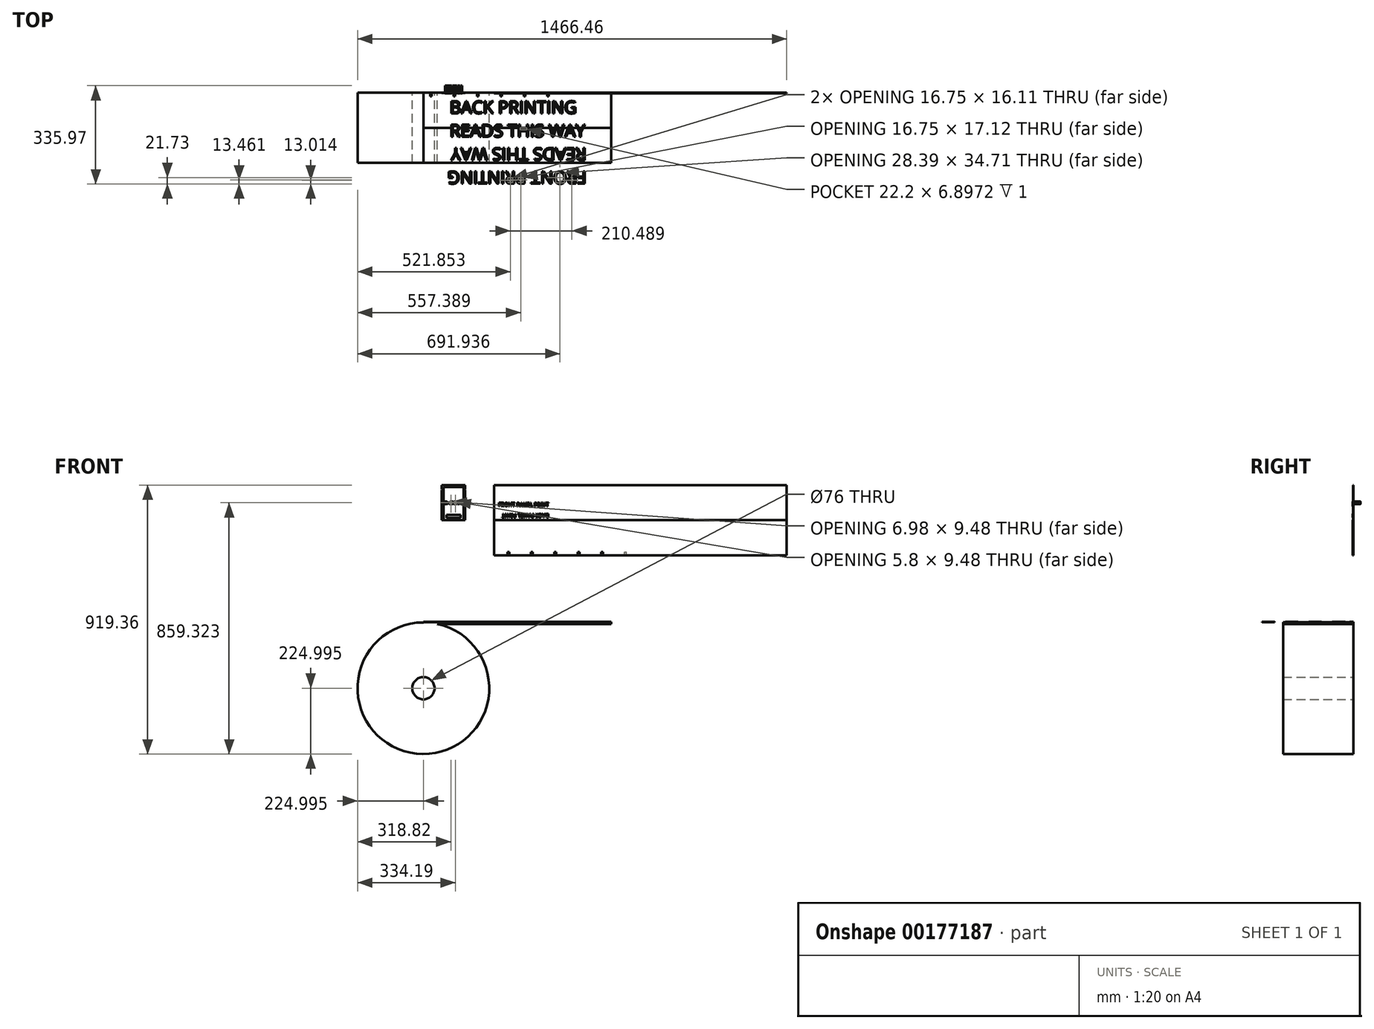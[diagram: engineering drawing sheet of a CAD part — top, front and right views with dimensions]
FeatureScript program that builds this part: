
annotation { "Feature Type Name" : "Feature", "Feature Type Description" : "" }
export const myFeature = defineFeature(function(context is Context, id is Id, definition is map)
    precondition{}
    {
        {
            assignVariable(context, id + "F0", {"name" : "hoogte", "anyValue" : 120});
        }
        {
            var Q0;
            Q0=qCreatedBy(makeId("Front.planeOp"),FACE);
            var sketch = newSketch(context, id + "F1", { "sketchPlane" : qUnion([Q0])});
            skLineSegment(sketch, "E0.bottom", {"start": v(-40, 60) * mm, "end": v(40, 60) * mm});
            skLineSegment(sketch, "E0.top", {"start": v(-40, -60) * mm, "end": v(40, -60) * mm});
            skLineSegment(sketch, "E0.left", {"start": v(-40, 60) * mm, "end": v(-40, -60) * mm});
            skLineSegment(sketch, "E0.right", {"start": v(40, 60) * mm, "end": v(40, -60) * mm});
            skLineSegment(sketch, "E1", {"start": v(-40, 46.41) * mm, "end": v(-38.59, 45) * mm});
            skLineSegment(sketch, "E2", {"start": v(-38.59, 45) * mm, "end": v(-40, 43.59) * mm});
            skLineSegment(sketch, "E3", {"start": v(40, 46.41) * mm, "end": v(38.59, 45) * mm});
            skLineSegment(sketch, "E4", {"start": v(38.59, 45) * mm, "end": v(40, 43.59) * mm});
            skLineSegment(sketch, "E5.bottom", {"start": v(138.46, 60) * mm, "end": v(1138.46, 60) * mm});
            skLineSegment(sketch, "E5.top", {"start": v(138.46, -180) * mm, "end": v(1138.46, -180) * mm});
            skLineSegment(sketch, "E5.left", {"start": v(138.46, 60) * mm, "end": v(138.46, -180) * mm});
            skLineSegment(sketch, "E5.right", {"start": v(1138.46, 60) * mm, "end": v(1138.46, -180) * mm});
            skLineSegment(sketch, "E6", {"start": v(138.46, -60) * mm, "end": v(1138.46, -60) * mm});
            skLineSegment(sketch, "E7", {"start": v(-40, 60) * mm, "end": v(40, -60) * mm, "construction": true});
            skLineSegment(sketch, "E8", {"start": v(40, 60) * mm, "end": v(-40, -60) * mm, "construction": true});
            skPoint(sketch, "E9", {"position": v(0, 0) * mm});
            skSolve(sketch);
        }
        {
            var Q0;
            {var subQ3=sQuery(id+"F1.wireOp",EDGE,"E0.bottom");Q0=makeQuery(id+"F1.imprint","IMPRINT",FACE,{"disambiguationData":[TD([[makeQuery(id+"F1.imprint","IMPRINT",EDGE,{"derivedFrom":subQ3}),-1.0]])]});}
            var Q1;
            Q1=makeQuery(id+"F1.imprint","IMPRINT",FACE,{"disambiguationData":[TD([[makeQuery(id+"F1.imprint","IMPRINT",EDGE,{"derivedFrom":sQuery(id+"F1.wireOp",EDGE,"E5.bottom")}),-1.0]])]});
            var Q2;
            {var subQ0=sQuery(id+"F1.wireOp",EDGE,"E5.top");Q2=makeQuery(id+"F1.imprint","IMPRINT",FACE,{"disambiguationData":[TD([[makeQuery(id+"F1.imprint","IMPRINT",EDGE,{"derivedFrom":subQ0}),1.0]])]});}
            extrude(context, id + "F2", {"entities" : qUnion([Q0, Q1, Q2]), "depth" : 1 * mm});
        }
        {
            var Q0;
            Q0=makeQuery(id+"F2.opExtrude","CAP_FACE",FACE,{"disambiguationData":[OSD([sQuery(id+"F1.wireOp",EDGE,"E0.bottom"),sQuery(id+"F1.wireOp",EDGE,"E0.top"),sQuery(id+"F1.wireOp",EDGE,"E0.left"),sQuery(id+"F1.wireOp",EDGE,"E0.right"),sQuery(id+"F1.wireOp",EDGE,"E1"),sQuery(id+"F1.wireOp",EDGE,"E2"),sQuery(id+"F1.wireOp",EDGE,"E3"),sQuery(id+"F1.wireOp",EDGE,"E4")])],"isStart":false});
            var sketch = newSketch(context, id + "F3", { "sketchPlane" : qUnion([Q0])});
            skLineSegment(sketch, "E10.0.0", {"start": v(40, 60) * mm, "end": v(-40, 60) * mm});
            skLineSegment(sketch, "E10.0.1", {"start": v(-40, 60) * mm, "end": v(-40, 46.41) * mm});
            skLineSegment(sketch, "E10.0.2", {"start": v(-40, 46.41) * mm, "end": v(-38.59, 45) * mm});
            skLineSegment(sketch, "E10.0.3", {"start": v(-38.59, 45) * mm, "end": v(-40, 43.59) * mm});
            skLineSegment(sketch, "E10.0.4", {"start": v(-40, 43.59) * mm, "end": v(-40, -60) * mm});
            skLineSegment(sketch, "E10.0.5", {"start": v(-40, -60) * mm, "end": v(40, -60) * mm});
            skLineSegment(sketch, "E10.0.6", {"start": v(40, -60) * mm, "end": v(40, 43.59) * mm});
            skLineSegment(sketch, "E10.0.7", {"start": v(40, 43.59) * mm, "end": v(38.59, 45) * mm});
            skLineSegment(sketch, "E10.0.8", {"start": v(38.59, 45) * mm, "end": v(40, 46.41) * mm});
            skLineSegment(sketch, "E10.0.9", {"start": v(40, 46.41) * mm, "end": v(40, 60) * mm});
            skLineSegment(sketch, "E11.bottom", {"start": v(-34, 54) * mm, "end": v(34, 54) * mm});
            skLineSegment(sketch, "E11.top", {"start": v(-34, -59.99) * mm, "end": v(34, -59.99) * mm});
            skLineSegment(sketch, "E11.left", {"start": v(-34, 54) * mm, "end": v(-34, -59.99) * mm});
            skLineSegment(sketch, "E11.right", {"start": v(34, 54) * mm, "end": v(34, -59.99) * mm});
            skLineSegment(sketch, "E12.bottom", {"start": v(-40, 60) * mm, "end": v(-37, 60) * mm});
            skLineSegment(sketch, "E12.top", {"start": v(-40, 48) * mm, "end": v(-37, 48) * mm});
            skLineSegment(sketch, "E12.left", {"start": v(-40, 60) * mm, "end": v(-40, 48) * mm});
            skLineSegment(sketch, "E12.right", {"start": v(-37, 60) * mm, "end": v(-37, 48) * mm});
            skLineSegment(sketch, "E13.bottom", {"start": v(40, 60) * mm, "end": v(37, 60) * mm});
            skLineSegment(sketch, "E13.top", {"start": v(40, 48) * mm, "end": v(37, 48) * mm});
            skLineSegment(sketch, "E13.left", {"start": v(40, 60) * mm, "end": v(40, 48) * mm});
            skLineSegment(sketch, "E13.right", {"start": v(37, 60) * mm, "end": v(37, 48) * mm});
            skLineSegment(sketch, "E14.bottom", {"start": v(-24, -42) * mm, "end": v(24, -42) * mm});
            skLineSegment(sketch, "E14.top", {"start": v(-24, -52) * mm, "end": v(24, -52) * mm});
            skLineSegment(sketch, "E14.left", {"start": v(-24, -42) * mm, "end": v(-24, -52) * mm});
            skLineSegment(sketch, "E14.right", {"start": v(24, -42) * mm, "end": v(24, -52) * mm});
            skSolve(sketch);
        }
        {
            var Q0;
            Q0=makeQuery(id+"F3.imprint","IMPRINT",FACE,{"disambiguationData":[TD([[makeQuery(id+"F3.imprint","IMPRINT",EDGE,{"derivedFrom":sQuery(id+"F3.wireOp",EDGE,"E11.bottom")}),-1.0]])]});
            var Q1;
            Q1=makeQuery(id+"F3.imprint","IMPRINT",FACE,{"disambiguationData":[TD([[makeQuery(id+"F3.imprint","IMPRINT",EDGE,{"derivedFrom":sQuery(id+"F3.wireOp",EDGE,"E12.bottom")}),-1.0]])]});
            var Q2;
            Q2=makeQuery(id+"F3.imprint","IMPRINT",FACE,{"disambiguationData":[TD([[makeQuery(id+"F3.imprint","IMPRINT",EDGE,{"derivedFrom":sQuery(id+"F3.wireOp",EDGE,"E13.bottom")}),-1.0]])]});
            extrude(context, id + "F4", {"entities" : qUnion([Q0, Q1, Q2]), "operationType" : NewBodyOperationType.REMOVE, "oppositeDirection" : true, "depth" : 0.5 * mm});
        }
        {
            var Q0;
            Q0=makeQuery(id+"F2.opExtrude","CAP_FACE",FACE,{"disambiguationData":[OSD([sQuery(id+"F1.wireOp",EDGE,"E5.bottom"),sQuery(id+"F1.wireOp",EDGE,"E5.left"),sQuery(id+"F1.wireOp",EDGE,"E5.right"),sQuery(id+"F1.wireOp",EDGE,"E6")])],"isStart":false});
            var sketch = newSketch(context, id + "F5", { "sketchPlane" : qUnion([Q0])});
            skLineSegment(sketch, "E15.0.0", {"start": v(1138.46, 60) * mm, "end": v(138.46, 60) * mm});
            skLineSegment(sketch, "E15.0.1", {"start": v(138.46, 60) * mm, "end": v(138.46, 60) * mm});
            skLineSegment(sketch, "E15.0.2", {"start": v(138.46, 60) * mm, "end": v(1138.46, 60) * mm});
            skLineSegment(sketch, "E15.0.3", {"start": v(1138.46, 60) * mm, "end": v(1138.46, 60) * mm});
            skLineSegment(sketch, "E16.bottom", {"start": v(184.68, -180) * mm, "end": v(190.68, -180) * mm});
            skLineSegment(sketch, "E16.top", {"start": v(184.68, -168) * mm, "end": v(190.68, -168) * mm});
            skLineSegment(sketch, "E16.left", {"start": v(184.68, -180) * mm, "end": v(184.68, -168) * mm});
            skLineSegment(sketch, "E16.right", {"start": v(190.68, -180) * mm, "end": v(190.68, -168) * mm});
            skLineSegment(sketch, "E17.1.0.0", {"start": v(264.68, -168) * mm, "end": v(270.68, -168) * mm});
            skLineSegment(sketch, "E17.1.0.1", {"start": v(264.68, -180) * mm, "end": v(264.68, -168) * mm});
            skLineSegment(sketch, "E17.1.0.2", {"start": v(264.68, -180) * mm, "end": v(270.68, -180) * mm});
            skLineSegment(sketch, "E17.1.0.3", {"start": v(270.68, -180) * mm, "end": v(270.68, -168) * mm});
            skLineSegment(sketch, "E17.2.0.0", {"start": v(344.68, -168) * mm, "end": v(350.68, -168) * mm});
            skLineSegment(sketch, "E17.2.0.1", {"start": v(344.68, -180) * mm, "end": v(344.68, -168) * mm});
            skLineSegment(sketch, "E17.2.0.2", {"start": v(344.68, -180) * mm, "end": v(350.68, -180) * mm});
            skLineSegment(sketch, "E17.2.0.3", {"start": v(350.68, -180) * mm, "end": v(350.68, -168) * mm});
            skLineSegment(sketch, "E17.direction1", {"start": v(184.68, -180) * mm, "end": v(264.68, -180) * mm, "construction": true});
            skLineSegment(sketch, "E18.0.3.0", {"start": v(424.68, -168) * mm, "end": v(430.68, -168) * mm});
            skLineSegment(sketch, "E18.3.3.0", {"start": v(424.68, -180) * mm, "end": v(424.68, -168) * mm});
            skLineSegment(sketch, "E18.6.3.0", {"start": v(424.68, -180) * mm, "end": v(430.68, -180) * mm});
            skLineSegment(sketch, "E18.9.3.0", {"start": v(430.68, -180) * mm, "end": v(430.68, -168) * mm});
            skLineSegment(sketch, "E18.0.4.0", {"start": v(504.68, -168) * mm, "end": v(510.68, -168) * mm});
            skLineSegment(sketch, "E18.3.4.0", {"start": v(504.68, -180) * mm, "end": v(504.68, -168) * mm});
            skLineSegment(sketch, "E18.6.4.0", {"start": v(504.68, -180) * mm, "end": v(510.68, -180) * mm});
            skLineSegment(sketch, "E18.9.4.0", {"start": v(510.68, -180) * mm, "end": v(510.68, -168) * mm});
            skLineSegment(sketch, "E19.0.5.0", {"start": v(584.68, -168) * mm, "end": v(590.68, -168) * mm});
            skLineSegment(sketch, "E19.3.5.0", {"start": v(584.68, -180) * mm, "end": v(584.68, -168) * mm});
            skLineSegment(sketch, "E19.6.5.0", {"start": v(584.68, -180) * mm, "end": v(590.68, -180) * mm});
            skLineSegment(sketch, "E19.9.5.0", {"start": v(590.68, -180) * mm, "end": v(590.68, -168) * mm});
            skSolve(sketch);
        }
        {
            var Q0;
            Q0=makeQuery(id+"F5.imprint","IMPRINT",FACE,{"disambiguationData":[TD([[makeQuery(id+"F5.imprint","IMPRINT",EDGE,{"derivedFrom":sQuery(id+"F5.wireOp",EDGE,"JLQzprwf-iRJq-cmRX-vWmS-HmgRmsplr5sc.top")}),-1.0]])]});
            var Q1;
            Q1=makeQuery(id+"F5.imprint","IMPRINT",FACE,{"disambiguationData":[TD([[makeQuery(id+"F5.imprint","IMPRINT",EDGE,{"derivedFrom":sQuery(id+"F5.wireOp",EDGE,"E16.bottom")}),1.0]])]});
            var Q2;
            Q2=makeQuery(id+"F5.imprint","IMPRINT",FACE,{"disambiguationData":[TD([[makeQuery(id+"F5.imprint","IMPRINT",EDGE,{"derivedFrom":sQuery(id+"F5.wireOp",EDGE,"E17.1.0.0")}),-1.0]])]});
            var Q3;
            Q3=makeQuery(id+"F5.imprint","IMPRINT",FACE,{"disambiguationData":[TD([[makeQuery(id+"F5.imprint","IMPRINT",EDGE,{"derivedFrom":sQuery(id+"F5.wireOp",EDGE,"E17.2.0.0")}),-1.0]])]});
            var Q4;
            Q4=makeQuery(id+"F5.imprint","IMPRINT",FACE,{"disambiguationData":[TD([[makeQuery(id+"F5.imprint","IMPRINT",EDGE,{"derivedFrom":sQuery(id+"F5.wireOp",EDGE,"E18.0.3.0")}),-1.0]])]});
            var Q5;
            Q5=makeQuery(id+"F5.imprint","IMPRINT",FACE,{"disambiguationData":[TD([[makeQuery(id+"F5.imprint","IMPRINT",EDGE,{"derivedFrom":sQuery(id+"F5.wireOp",EDGE,"E18.0.4.0")}),-1.0]])]});
            var Q6;
            Q6=makeQuery(id+"F5.imprint","IMPRINT",FACE,{"disambiguationData":[TD([[makeQuery(id+"F5.imprint","IMPRINT",EDGE,{"derivedFrom":sQuery(id+"F5.wireOp",EDGE,"E19.0.5.0")}),-1.0]])]});
            extrude(context, id + "F6", {"entities" : qUnion([Q0, Q1, Q2, Q3, Q4, Q5, Q6]), "operationType" : NewBodyOperationType.REMOVE, "oppositeDirection" : true, "depth" : 0.5 * mm});
        }
        {
            var Q0;
            Q0=qCreatedBy(makeId("Front.planeOp"),FACE);
            var sketch = newSketch(context, id + "F7", { "sketchPlane" : qUnion([Q0])});
            skCircle(sketch, "E20", {"center": v(-103, -634.36) * mm, "radius": 225 * mm});
            skLineSegment(sketch, "E21.bottom", {"start": v(-103, -408.35) * mm, "end": v(538.87, -408.35) * mm});
            skLineSegment(sketch, "E21.top", {"start": v(-103, -414.51) * mm, "end": v(538.87, -414.51) * mm});
            skLineSegment(sketch, "E21.left", {"start": v(-103, -414.51) * mm, "end": v(-103, -408.35) * mm});
            skLineSegment(sketch, "E21.right", {"start": v(538.87, -414.51) * mm, "end": v(538.87, -408.35) * mm});
            skCircle(sketch, "E22", {"center": v(-103, -634.36) * mm, "radius": 38 * mm});
            skSolve(sketch);
        }
        {
            var Q0;
            Q0=qSketchRegion(id+"F7",true);
            extrude(context, id + "F8", {"entities" : qUnion([Q0]), "depth" : (((getVariable(context, 'hoogte')) * 2)) * mm});
        }
        {
            var Q0;
            {var subQ0=sQuery(id+"F1.wireOp",EDGE,"E4");var subQ1=sQuery(id+"F1.wireOp",EDGE,"E2");var subQ2=sQuery(id+"F1.wireOp",EDGE,"E1");var subQ3=sQuery(id+"F1.wireOp",EDGE,"E0.right");var subQ4=sQuery(id+"F1.wireOp",EDGE,"E0.top");var subQ5=sQuery(id+"F1.wireOp",EDGE,"E0.bottom");var subQ6=sQuery(id+"F1.wireOp",EDGE,"E3");var subQ7=sQuery(id+"F1.wireOp",EDGE,"E0.left");Q0=makeQuery(id+"F4.boolean.opBoolean","SPLIT",FACE,{"disambiguationData":[TD([makeQuery(id+"F2.opExtrude","SWEPT_FACE",FACE,{"disambiguationData":[OSD([subQ5])]})])],"derivedFrom":makeQuery(id+"F2.opExtrude","CAP_FACE",FACE,{"disambiguationData":[OSD([subQ5,subQ4,subQ7,subQ3,subQ2,subQ1,subQ6,subQ0])],"isStart":false})});}
            var sketch = newSketch(context, id + "F9", { "sketchPlane" : qUnion([Q0])});
            skText(sketch, "E23", { "text": "BACKSIDE", "fontName": "OpenSans-Regular.ttf"});
            const initialGuessF9  = {"E23": [-0.03, -0.00465, 1, 0, 0.0093]};
            skSetInitialGuess(sketch, initialGuessF9);
            skSolve(sketch);
        }
        {
            var Q0;
            Q0=qSketchRegion(id+"F9",true);
            extrude(context, id + "F10", {"entities" : qUnion([Q0]), "operationType" : NewBodyOperationType.ADD, "depth" : 1 * mm, "hasSecondDirection" : true, "secondDirectionOppositeDirection" : true, "secondDirectionDepth" : 25 * mm});
        }
        {
            var Q0;
            {var subQ0=sQuery(id+"F1.wireOp",EDGE,"E5.bottom");var subQ1=sQuery(id+"F1.wireOp",EDGE,"E5.left");var subQ2=sQuery(id+"F1.wireOp",EDGE,"E5.right");Q0=makeQuery(id+"F6.boolean.opBoolean","SPLIT",FACE,{"disambiguationData":[TD([makeQuery(id+"F2.opExtrude","SWEPT_FACE",FACE,{"disambiguationData":[OSD([subQ0])]})])],"derivedFrom":makeQuery(id+"F2.opExtrude","CAP_FACE",FACE,{"disambiguationData":[OSD([subQ0,sQuery(id+"F1.wireOp",EDGE,"E5.top"),subQ1,subQ2])],"isStart":false})});}
            var sketch = newSketch(context, id + "F11", { "sketchPlane" : qUnion([Q0])});
            skText(sketch, "E24", { "text": "FRONT PANEL PRINT", "fontName": "AllertaStencil-Regular.ttf"});
            skLineSegment(sketch, "E25.0.0", {"start": v(1138.46, -60) * mm, "end": v(138.46, -60) * mm});
            skLineSegment(sketch, "E25.0.1", {"start": v(138.46, -60) * mm, "end": v(138.46, -180) * mm});
            skLineSegment(sketch, "E25.0.2", {"start": v(138.46, -180) * mm, "end": v(184.68, -180) * mm});
            skLineSegment(sketch, "E25.0.3", {"start": v(184.68, -180) * mm, "end": v(184.68, -168) * mm});
            skLineSegment(sketch, "E25.0.4", {"start": v(184.68, -168) * mm, "end": v(190.68, -168) * mm});
            skLineSegment(sketch, "E25.0.5", {"start": v(190.68, -168) * mm, "end": v(190.68, -180) * mm});
            skLineSegment(sketch, "E25.0.6", {"start": v(190.68, -180) * mm, "end": v(264.68, -180) * mm});
            skLineSegment(sketch, "E25.0.7", {"start": v(264.68, -180) * mm, "end": v(264.68, -168) * mm});
            skLineSegment(sketch, "E25.0.8", {"start": v(264.68, -168) * mm, "end": v(270.68, -168) * mm});
            skLineSegment(sketch, "E25.0.9", {"start": v(270.68, -168) * mm, "end": v(270.68, -180) * mm});
            skLineSegment(sketch, "E25.0.10", {"start": v(270.68, -180) * mm, "end": v(344.68, -180) * mm});
            skLineSegment(sketch, "E25.0.11", {"start": v(344.68, -180) * mm, "end": v(344.68, -168) * mm});
            skLineSegment(sketch, "E25.0.12", {"start": v(344.68, -168) * mm, "end": v(350.68, -168) * mm});
            skLineSegment(sketch, "E25.0.13", {"start": v(350.68, -168) * mm, "end": v(350.68, -180) * mm});
            skLineSegment(sketch, "E25.0.14", {"start": v(350.68, -180) * mm, "end": v(424.68, -180) * mm});
            skLineSegment(sketch, "E25.0.15", {"start": v(424.68, -180) * mm, "end": v(424.68, -168) * mm});
            skLineSegment(sketch, "E25.0.16", {"start": v(424.68, -168) * mm, "end": v(430.68, -168) * mm});
            skLineSegment(sketch, "E25.0.17", {"start": v(430.68, -168) * mm, "end": v(430.68, -180) * mm});
            skLineSegment(sketch, "E25.0.18", {"start": v(430.68, -180) * mm, "end": v(504.68, -180) * mm});
            skLineSegment(sketch, "E25.0.19", {"start": v(504.68, -180) * mm, "end": v(504.68, -168) * mm});
            skLineSegment(sketch, "E25.0.20", {"start": v(504.68, -168) * mm, "end": v(510.68, -168) * mm});
            skLineSegment(sketch, "E25.0.21", {"start": v(510.68, -168) * mm, "end": v(510.68, -180) * mm});
            skLineSegment(sketch, "E25.0.22", {"start": v(510.68, -180) * mm, "end": v(1138.46, -180) * mm});
            skLineSegment(sketch, "E25.0.23", {"start": v(1138.46, -180) * mm, "end": v(1138.46, -60) * mm});
            skText(sketch, "E26", { "text": "BACK PANEL PRINT", "fontName": "AllertaStencil-Regular.ttf"});
            skLineSegment(sketch, "E27", {"start": v(1108.46, -120) * mm, "end": v(1108.46, -121.37) * mm});
            const initialGuessF11  = {"E24": [0.1529, -0.0125, 1, 0, 0.0125], "E26": [0.32596, -0.0375, -1, 0, 0.0125]};
            skSetInitialGuess(sketch, initialGuessF11);
            skSolve(sketch);
        }
        {
            var Q0;
            Q0=qSketchRegion(id+"F11",true);
            extrude(context, id + "F12", {"entities" : qUnion([Q0]), "operationType" : NewBodyOperationType.ADD, "depth" : 1 * mm});
        }
        {
            var Q0;
            Q0=makeQuery(id+"F8.opExtrude","SWEPT_FACE",FACE,{"disambiguationData":[OSD([sQuery(id+"F7.wireOp",EDGE,"E21.bottom")])]});
            var sketch = newSketch(context, id + "F13", { "sketchPlane" : qUnion([Q0])});
            skText(sketch, "E28", { "text": "BACK PRINTING \nREADS THIS WAY", "fontName": "OpenSans-Regular.ttf"});
            skText(sketch, "E29", { "text": "FRONT PRINTING\nREADS THIS WAY", "fontName": "OpenSans-Regular.ttf"});
            skLineSegment(sketch, "E30", {"start": v(478.87, -157.44) * mm, "end": v(478.87, -220) * mm});
            skLineSegment(sketch, "E31", {"start": v(538.87, -120) * mm, "end": v(-103, -120) * mm, "construction": true});
            skLineSegment(sketch, "E32.bottom", {"start": v(538.87, -120) * mm, "end": v(-103, -120) * mm});
            skLineSegment(sketch, "E32.top", {"start": v(538.87, -119.95) * mm, "end": v(-103, -119.95) * mm});
            skLineSegment(sketch, "E32.left", {"start": v(538.87, -120) * mm, "end": v(538.87, -119.95) * mm});
            skLineSegment(sketch, "E32.right", {"start": v(-103, -120) * mm, "end": v(-103, -119.95) * mm});
            skLineSegment(sketch, "E33.bottom", {"start": v(538.87, -120.05) * mm, "end": v(-103, -120.05) * mm});
            skLineSegment(sketch, "E33.left", {"start": v(538.87, -120.05) * mm, "end": v(538.87, -120) * mm});
            skLineSegment(sketch, "E33.right", {"start": v(-103, -120.05) * mm, "end": v(-103, -120) * mm});
            skLineSegment(sketch, "E34.bottom", {"start": v(-80.23, 0) * mm, "end": v(-74.23, 0) * mm});
            skLineSegment(sketch, "E34.top", {"start": v(-80.23, -12) * mm, "end": v(-74.23, -12) * mm});
            skLineSegment(sketch, "E34.left", {"start": v(-80.23, 0) * mm, "end": v(-80.23, -12) * mm});
            skLineSegment(sketch, "E34.right", {"start": v(-74.23, 0) * mm, "end": v(-74.23, -12) * mm});
            skLineSegment(sketch, "E35.1.0.0", {"start": v(-0.23, 0) * mm, "end": v(5.77, 0) * mm});
            skLineSegment(sketch, "E35.1.0.1", {"start": v(-0.23, -12) * mm, "end": v(5.77, -12) * mm});
            skLineSegment(sketch, "E35.1.0.2", {"start": v(-0.23, 0) * mm, "end": v(-0.23, -12) * mm});
            skLineSegment(sketch, "E35.1.0.3", {"start": v(5.77, 0) * mm, "end": v(5.77, -12) * mm});
            skLineSegment(sketch, "E35.2.0.0", {"start": v(79.77, 0) * mm, "end": v(85.77, 0) * mm});
            skLineSegment(sketch, "E35.2.0.1", {"start": v(79.77, -12) * mm, "end": v(85.77, -12) * mm});
            skLineSegment(sketch, "E35.2.0.2", {"start": v(79.77, 0) * mm, "end": v(79.77, -12) * mm});
            skLineSegment(sketch, "E35.2.0.3", {"start": v(85.77, 0) * mm, "end": v(85.77, -12) * mm});
            skLineSegment(sketch, "E35.direction1", {"start": v(-80.23, -12) * mm, "end": v(-0.23, -12) * mm, "construction": true});
            skLineSegment(sketch, "E36.0.3.0", {"start": v(159.77, 0) * mm, "end": v(165.77, 0) * mm});
            skLineSegment(sketch, "E36.3.3.0", {"start": v(159.77, -12) * mm, "end": v(165.77, -12) * mm});
            skLineSegment(sketch, "E36.6.3.0", {"start": v(159.77, 0) * mm, "end": v(159.77, -12) * mm});
            skLineSegment(sketch, "E36.9.3.0", {"start": v(165.77, 0) * mm, "end": v(165.77, -12) * mm});
            skLineSegment(sketch, "E36.0.4.0", {"start": v(239.77, 0) * mm, "end": v(245.77, 0) * mm});
            skLineSegment(sketch, "E36.3.4.0", {"start": v(239.77, -12) * mm, "end": v(245.77, -12) * mm});
            skLineSegment(sketch, "E36.6.4.0", {"start": v(239.77, 0) * mm, "end": v(239.77, -12) * mm});
            skLineSegment(sketch, "E36.9.4.0", {"start": v(245.77, 0) * mm, "end": v(245.77, -12) * mm});
            skLineSegment(sketch, "E36.0.5.0", {"start": v(319.77, 0) * mm, "end": v(325.77, 0) * mm});
            skLineSegment(sketch, "E36.3.5.0", {"start": v(319.77, -12) * mm, "end": v(325.77, -12) * mm});
            skLineSegment(sketch, "E36.6.5.0", {"start": v(319.77, 0) * mm, "end": v(319.77, -12) * mm});
            skLineSegment(sketch, "E36.9.5.0", {"start": v(325.77, 0) * mm, "end": v(325.77, -12) * mm});
            const initialGuessF13  = {"E28": [-0.01285, -0.07083, 1, 0, 0.0425], "E29": [0.45387, -0.26917, -1, 0, 0.0425]};
            skSetInitialGuess(sketch, initialGuessF13);
            skSolve(sketch);
        }
        {
            var Q0;
            Q0=qSketchRegion(id+"F13",true);
            extrude(context, id + "F14", {"entities" : qUnion([Q0]), "operationType" : NewBodyOperationType.ADD, "depth" : 1 * mm});
        }
    });
